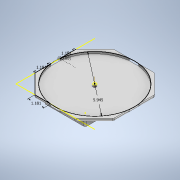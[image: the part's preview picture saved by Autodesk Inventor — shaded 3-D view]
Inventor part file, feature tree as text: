
AUTODESK INVENTOR PART (.ipt)
format: ipt  version: 2020 (Build 240168000, 168)  size: 200,192 bytes
history: native  units: in
note: dims shown in document units (in); Inventor stores cm internally (conversion verified against a paired STEP export)
features: extrude x4, sketch x4, hole x2, other x1, pattern_circular x1, fillet x1
ambient origin geometry x8: Origin, YZ Plane, XZ Plane, XY Plane, X Axis, Y Axis, Z Axis, Center Point
bodies: Solid1 (feature_tree)
feature tree (13):
  extrude  "Extrusion1"  Depth=4.4882in
  sketch  "Sketch2"  dims[d2=0.689in d3=0.0in]
  hole  "Hole1"  [1 undecoded]
  hole  "Hole2"  [1 undecoded]
  extrude  "Extrusion2"  Depth=0.125in TaperAngle=0.0deg
  sketch  "Sketch4"  dims[d11=0.1378in d12=0.75in d13=0.375in d14=0.25in d15=0.5635in d16=0.6201in d17=0.8108in d18=5.9055in d19=5.9055in d20=0.2362in d21=0.0in d22=5.9449in d23=0.1575in d24=0.0in d25=1.1811in d26=1.1811in d27=90.0deg d28=1.1811in d29=0.2362in d30=0.0in d31=1.5748in d32=360.0deg d34=0.125in]
  extrude  "Extrusion3"  Depth=0.125in
  extrude  "Extrusion4"  Depth=0.125in TaperAngle=0.0deg
  other  "Work Axis1"
  pattern_circular  "Circular Pattern1"  Count=3  [1 undecoded]
  fillet  "Fillet1"  Radius=1.1811in
  sketch  "Sketch1"  dims[d0=3.0709in d1=4.4882in]
  sketch  "Sketch3"  dims[d4=0.2362in d5=0.75in d6=0.375in d7=0.25in d8=0.5635in d9=0.6201in d10=0.8108in]
note: 3 required parameter values undecoded (feature->parameter linkage not recoverable at this tier; creation-order binding heuristic only, values carry confidence <= 0.55)
